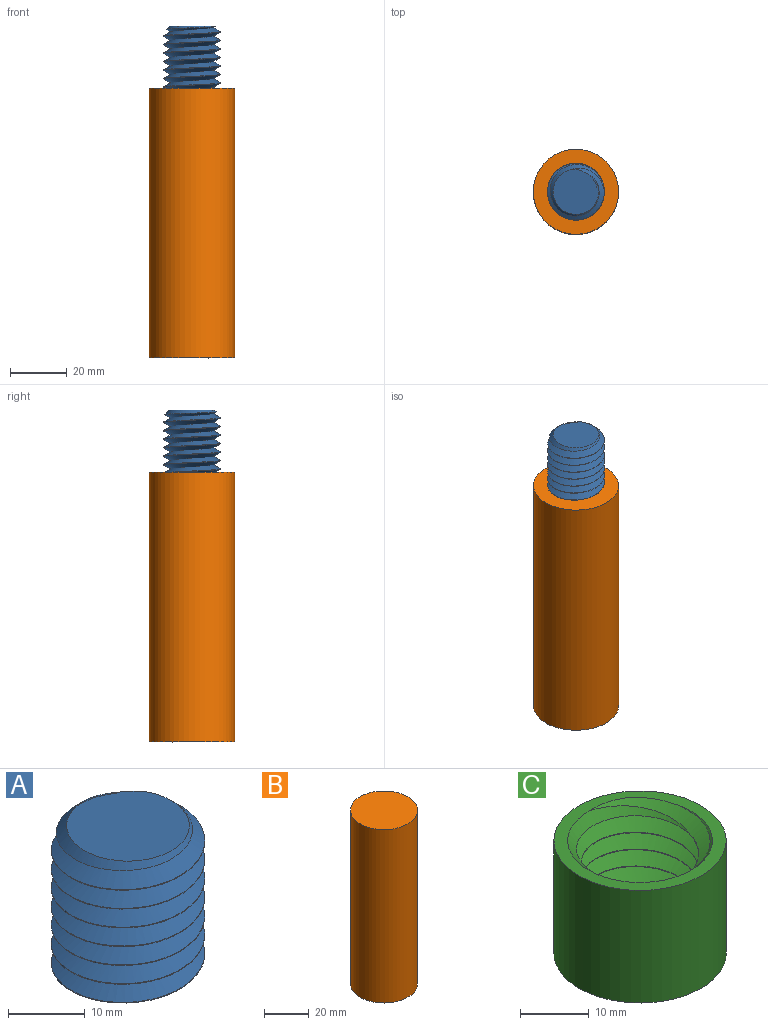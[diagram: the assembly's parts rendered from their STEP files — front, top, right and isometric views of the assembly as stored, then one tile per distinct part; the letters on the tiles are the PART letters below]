
ASSEMBLY  parts=3 mates=2
PART A: 6 faces, bbox 22x25.1x27.5 mm
  f0: cylinder r=10mm len=20mm, axis (0,0,-1), area -70.8mm2, adj f2,f3,f4,f5
  f1: plane 16.18x16.07mm, normal (0,0,1), area 198.6mm2, adj f3,f4,f5
  f2: plane 19.72x19.7mm, normal (0,0,-1), area 244.2mm2, adj f0,f4,f5
  f3: cone r=8mm half-angle=45deg, axis (0,0,-1), area 64.7mm2, adj f0,f1,f4,f5
  f4: bspline ~23.95x23.09mm, area 1129.6mm2, adj f0,f1,f2,f3,f5
  f5: bspline ~25.45x23.09mm, area 1124.5mm2, adj f0,f1,f2,f3,f4
PART B: 5 faces, bbox 30x30x95 mm
  f0: cylinder r=15mm len=95mm, axis (0,0,-1), area 8953.5mm2, adj f1,f2
  f1: plane 30x30mm, normal (0,0,1), area 706.9mm2, adj f0
  f2: plane 30x30mm, normal (0,0,-1), area 392.7mm2, adj f0,f3
  f3: cylinder r=10mm len=25mm, axis (0,0,1), area 1570.8mm2, adj f2,f4
  f4: sphere r=10mm, area 628.3mm2, adj f3
PART C: 7 faces, bbox 27x27.4x25.4 mm
  f0: cylinder r=8.5mm len=18mm, axis (0,0,-1), area 28mm2, adj f3,f4,f5,f6
  f1: cylinder r=12.5mm len=25mm, axis (0,0,-1), area 1570.8mm2, adj f2,f3
  f2: plane 25.08x25.08mm, normal (0,0,1), area 141.1mm2, adj f1,f4,f5,f6
  f3: plane 27x27mm, normal (0,0,-1), area 192.7mm2, adj f0,f1,f5,f6
  f4: cone r=8.5mm half-angle=45deg, axis (0,0,1), area 73mm2, adj f0,f2,f5,f6
  f5: bspline ~25.43x22.95mm, area 1132mm2, adj f0,f2,f3,f4,f6
  f6: bspline ~25.43x22.45mm, area 1141.3mm2, adj f0,f2,f3,f4,f5
PLACE A t=(-105.18,51.6,196.78)mm
PLACE B t=(-44.64,51.6,11.78)mm
PLACE C t=(-105.18,51.6,101.78)mm
MATE fastened C.f1 <-> B.f0  axis (0,0,-1) through (-105.18,51.6,101.78)mm
MATE fastened A.f0 <-> B.f0  axis (0,0,-1) through (-105.18,51.6,196.78)mm
